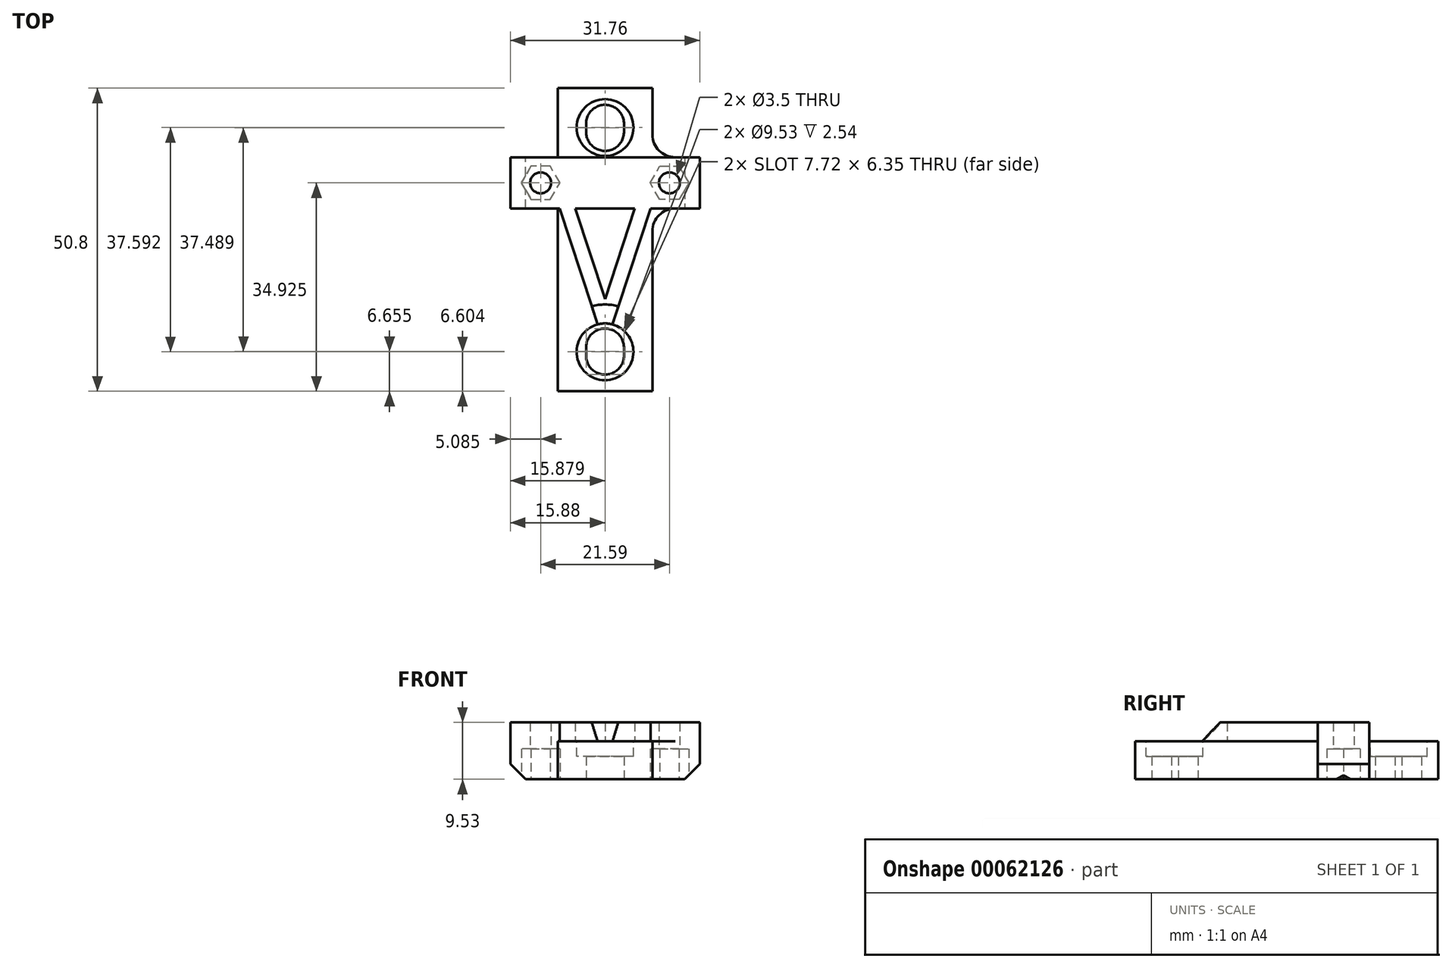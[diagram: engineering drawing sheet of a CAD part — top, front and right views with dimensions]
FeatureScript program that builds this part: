
annotation { "Feature Type Name" : "Feature", "Feature Type Description" : "" }
export const myFeature = defineFeature(function(context is Context, id is Id, definition is map)
    precondition{}
    {
        {
            var Q0;
            Q0=qCreatedBy(makeId("Top.planeOp"),FACE);
            var sketch = newSketch(context, id + "F0", { "sketchPlane" : qUnion([Q0])});
            skLineSegment(sketch, "E0.bottom", {"start": v(-7.94, 25.4) * mm, "end": v(7.94, 25.4) * mm});
            skLineSegment(sketch, "E0.top", {"start": v(-7.94, -25.4) * mm, "end": v(7.94, -25.4) * mm});
            skLineSegment(sketch, "E0.left", {"start": v(-7.94, 25.4) * mm, "end": v(-7.94, -25.4) * mm});
            skLineSegment(sketch, "E0.right", {"start": v(7.94, 25.4) * mm, "end": v(7.94, -25.4) * mm});
            skPoint(sketch, "E1", {"position": v(0, 18.8) * mm});
            skPoint(sketch, "E2", {"position": v(0, -18.8) * mm});
            skLineSegment(sketch, "E3", {"start": v(3.17, -18.16) * mm, "end": v(3.17, -19.43) * mm});
            skArc(sketch, "E4", {"start": v(3.17, -19.43) * mm, "mid": v(-0.05, -22.6) * mm, "end": v(-3.17, -19.33) * mm});
            skLineSegment(sketch, "E5", {"start": v(0, -28.7) * mm, "end": v(0, 36.3) * mm, "construction": true});
            skLineSegment(sketch, "E6", {"start": v(-3.17, -19.33) * mm, "end": v(-3.17, -18.06) * mm});
            skArc(sketch, "E7", {"start": v(-3.17, -18.06) * mm, "mid": v(0.05, -14.88) * mm, "end": v(3.17, -18.16) * mm});
            skLineSegment(sketch, "E8.MirrorCS", {"start": v(-7.94, -25.4) * mm, "end": v(-7.94, 25.4) * mm});
            skArc(sketch, "E9.MirrorCS", {"start": v(-3.17, 18.06) * mm, "mid": v(0.05, 14.88) * mm, "end": v(3.17, 18.16) * mm});
            skLineSegment(sketch, "E10.MirrorCS", {"start": v(-3.17, 19.33) * mm, "end": v(-3.17, 18.06) * mm});
            skArc(sketch, "E11.MirrorCS", {"start": v(3.17, 19.43) * mm, "mid": v(-0.05, 22.6) * mm, "end": v(-3.17, 19.33) * mm});
            skLineSegment(sketch, "E12.MirrorCS", {"start": v(3.17, 18.16) * mm, "end": v(3.17, 19.43) * mm});
            skSolve(sketch);
        }
        {
            var Q0;
            Q0 = qSketchRegion(id + "F0", true);
            extrude(context, id + "F1", {"entities" : qUnion([Q0]), "depth" : 6.35 * mm});
        }
        {
            var Q0;
            Q0=makeQuery(id+"F1.opExtrude","CAP_FACE",FACE,{"disambiguationData":[OSD([sQuery(id+"F0.wireOp",EDGE,"E0.bottom"),sQuery(id+"F0.wireOp",EDGE,"E0.top"),sQuery(id+"F0.wireOp",EDGE,"E0.left"),sQuery(id+"F0.wireOp",EDGE,"E0.right"),sQuery(id+"F0.wireOp",EDGE,"db3065ad-5405-4db5-aa4e-17a35d9fe363"),sQuery(id+"F0.wireOp",EDGE,"fdb6fcd1-f64e-4614-bf4e-cf34bd7a5e28")])],"isStart":false});
            var sketch = newSketch(context, id + "F2", { "sketchPlane" : qUnion([Q0])});
            skLineSegment(sketch, "E13.bottom", {"start": v(-15.88, 13.83) * mm, "end": v(15.88, 13.83) * mm});
            skLineSegment(sketch, "E13.top", {"start": v(-15.87, 5.23) * mm, "end": v(15.87, 5.23) * mm});
            skLineSegment(sketch, "E13.left", {"start": v(-15.88, 13.83) * mm, "end": v(-15.88, 5.22) * mm});
            skLineSegment(sketch, "E13.right", {"start": v(15.88, 13.83) * mm, "end": v(15.88, 5.22) * mm});
            skLineSegment(sketch, "E14", {"start": v(-31.76, 9.52) * mm, "end": v(36.02, 9.53) * mm, "construction": true});
            skCircle(sketch, "E15", {"center": v(-10.8, 9.52) * mm, "radius": 1.75 * mm});
            skCircle(sketch, "E16", {"center": v(10.8, 9.52) * mm, "radius": 1.75 * mm});
            skSolve(sketch);
        }
        {
            var Q0;
            Q0 = qSketchRegion(id + "F2", true);
            var Q1;
            Q1=makeQuery(id+"F1.opExtrude","CAP_FACE",FACE,{"disambiguationData":[OSD([sQuery(id+"F0.wireOp",EDGE,"E0.bottom"),sQuery(id+"F0.wireOp",EDGE,"E0.top"),sQuery(id+"F0.wireOp",EDGE,"E0.left"),sQuery(id+"F0.wireOp",EDGE,"E0.right"),sQuery(id+"F0.wireOp",EDGE,"db3065ad-5405-4db5-aa4e-17a35d9fe363"),sQuery(id+"F0.wireOp",EDGE,"fdb6fcd1-f64e-4614-bf4e-cf34bd7a5e28")])],"isStart":true});
            extrude(context, id + "F3", {"entities" : qUnion([Q0]), "operationType" : NewBodyOperationType.ADD, "depth" : 3.17 * mm, "hasSecondDirection" : true, "secondDirectionBound" : SecondDirectionBoundingType.UP_TO_SURFACE, "secondDirectionOppositeDirection" : true, "secondDirectionBoundEntityFace" : qUnion([Q1]), "secondDirectionDepth" : 25.4 * mm});
        }
        {
            var Q0;
            {var subQ0=sQuery(id+"F0.wireOp",EDGE,"E3");var subQ1=sQuery(id+"F0.wireOp",EDGE,"E0.right");var subQ2=sQuery(id+"F0.wireOp",EDGE,"E4");var subQ3=sQuery(id+"F0.wireOp",EDGE,"E0.top");var subQ4=sQuery(id+"F0.wireOp",EDGE,"E6");var subQ5=sQuery(id+"F0.wireOp",EDGE,"E7");var subQ6=sQuery(id+"F0.wireOp",EDGE,"E8.MirrorCS");Q0=makeQuery(id+"F3.boolean.opBoolean","SPLIT",FACE,{"disambiguationData":[TD([makeQuery(id+"F1.opExtrude","SWEPT_FACE",FACE,{"disambiguationData":[OSD([subQ3])]})])],"derivedFrom":makeQuery(id+"F1.opExtrude","CAP_FACE",FACE,{"disambiguationData":[OSD([subQ3,subQ1,subQ0,subQ2,subQ4,subQ5,subQ6,sQuery(id+"F0.wireOp",EDGE,"E0.bottom"),sQuery(id+"F0.wireOp",EDGE,"E9.MirrorCS"),sQuery(id+"F0.wireOp",EDGE,"E10.MirrorCS"),sQuery(id+"F0.wireOp",EDGE,"E11.MirrorCS"),sQuery(id+"F0.wireOp",EDGE,"E12.MirrorCS")])],"isStart":false})});}
            var sketch = newSketch(context, id + "F4", { "sketchPlane" : qUnion([Q0])});
            skCircle(sketch, "E17", {"center": v(0, -18.8) * mm, "radius": 4.76 * mm});
            skCircle(sketch, "E18", {"center": v(0, 18.8) * mm, "radius": 4.76 * mm});
            skSolve(sketch);
        }
        {
            var Q0;
            Q0 = qSketchRegion(id + "F4", true);
            extrude(context, id + "F5", {"entities" : qUnion([Q0]), "operationType" : NewBodyOperationType.REMOVE, "oppositeDirection" : true, "depth" : 2.54 * mm});
        }
        {
            var Q0;
            Q0=makeQuery(id+"F3.opExtrude","CAP_EDGE",EDGE,{"disambiguationData":[OSD([sQuery(id+"F2.wireOp",EDGE,"E13.left")])],"isStart":true});
            var Q1;
            Q1=makeQuery(id+"F3.opExtrude","CAP_EDGE",EDGE,{"disambiguationData":[OSD([sQuery(id+"F2.wireOp",EDGE,"E13.right")])],"isStart":true});
            chamfer(context, id + "F6", {"entities" : qUnion([Q0, Q1]), "width" : 2.54 * mm, "tangentPropagation" : true});
        }
        {
            var Q0;
            Q0=makeQuery(id+"F3.boolean.opBoolean","MERGE",FACE,{"derivedFrom":[makeQuery(id+"F1.opExtrude","CAP_FACE",FACE,{"disambiguationData":[OSD([sQuery(id+"F0.wireOp",EDGE,"E0.top"),sQuery(id+"F0.wireOp",EDGE,"E0.right"),sQuery(id+"F0.wireOp",EDGE,"E3"),sQuery(id+"F0.wireOp",EDGE,"E4"),sQuery(id+"F0.wireOp",EDGE,"E6"),sQuery(id+"F0.wireOp",EDGE,"E7"),sQuery(id+"F0.wireOp",EDGE,"E8.MirrorCS"),sQuery(id+"F0.wireOp",EDGE,"E0.bottom"),sQuery(id+"F0.wireOp",EDGE,"E9.MirrorCS"),sQuery(id+"F0.wireOp",EDGE,"E10.MirrorCS"),sQuery(id+"F0.wireOp",EDGE,"E11.MirrorCS"),sQuery(id+"F0.wireOp",EDGE,"E12.MirrorCS")])],"isStart":true}),makeQuery(id+"F3.opExtrude","CAP_FACE",FACE,{"disambiguationData":[OSD([sQuery(id+"F2.wireOp",EDGE,"E13.bottom"),sQuery(id+"F2.wireOp",EDGE,"E13.top"),sQuery(id+"F2.wireOp",EDGE,"E13.left"),sQuery(id+"F2.wireOp",EDGE,"E13.right"),sQuery(id+"F2.wireOp",EDGE,"E15"),sQuery(id+"F2.wireOp",EDGE,"E16")])],"isStart":true})]});
            var sketch = newSketch(context, id + "F7", { "sketchPlane" : qUnion([Q0])});
            skCircle(sketch, "E19.cCircle", {"center": v(-10.8, -9.52) * mm, "radius": 2.8 * mm, "construction": true});
            skLineSegment(sketch, "E19.0", {"start": v(-7.57, -9.53) * mm, "end": v(-9.18, -12.32) * mm});
            skLineSegment(sketch, "E19.1", {"start": v(-9.18, -12.32) * mm, "end": v(-12.4, -12.32) * mm});
            skLineSegment(sketch, "E19.2", {"start": v(-12.4, -12.32) * mm, "end": v(-14.02, -9.52) * mm});
            skLineSegment(sketch, "E19.3", {"start": v(-14.02, -9.52) * mm, "end": v(-12.4, -6.73) * mm});
            skLineSegment(sketch, "E19.4", {"start": v(-12.4, -6.73) * mm, "end": v(-9.18, -6.73) * mm});
            skLineSegment(sketch, "E19.5", {"start": v(-9.18, -6.73) * mm, "end": v(-7.57, -9.53) * mm});
            skPoint(sketch, "E19.0.midPoint", {"position": v(-8.38, -10.92) * mm});
            skLineSegment(sketch, "E20.MirrorCS", {"start": v(9.18, -6.73) * mm, "end": v(7.57, -9.53) * mm});
            skLineSegment(sketch, "E21.MirrorCS", {"start": v(12.4, -6.73) * mm, "end": v(9.18, -6.73) * mm});
            skLineSegment(sketch, "E22.MirrorCS", {"start": v(14.02, -9.52) * mm, "end": v(12.4, -6.73) * mm});
            skLineSegment(sketch, "E23.MirrorCS", {"start": v(12.4, -12.32) * mm, "end": v(14.02, -9.52) * mm});
            skLineSegment(sketch, "E24.MirrorCS", {"start": v(9.18, -12.32) * mm, "end": v(12.4, -12.32) * mm});
            skLineSegment(sketch, "E25.MirrorCS", {"start": v(7.57, -9.53) * mm, "end": v(9.18, -12.32) * mm});
            skCircle(sketch, "E26.MirrorC", {"center": v(10.8, -9.52) * mm, "radius": 2.8 * mm, "construction": true});
            skSolve(sketch);
        }
        {
            var Q0;
            Q0 = qSketchRegion(id + "F7", true);
            extrude(context, id + "F8", {"entities" : qUnion([Q0]), "operationType" : NewBodyOperationType.REMOVE, "oppositeDirection" : true, "depth" : 5.08 * mm});
        }
        {
            var Q0;
            Q0=makeQuery(id+"F3.boolean.opBoolean","INTERSECT",EDGE,{"derivedFrom":[makeQuery(id+"F1.opExtrude","SWEPT_FACE",FACE,{"disambiguationData":[OSD([sQuery(id+"F0.wireOp",EDGE,"E8.MirrorCS")])]}),makeQuery(id+"F3.opExtrude","SWEPT_FACE",FACE,{"disambiguationData":[OSD([sQuery(id+"F2.wireOp",EDGE,"E13.top")])]})]});
            var Q1;
            Q1=makeQuery(id+"F3.boolean.opBoolean","INTERSECT",EDGE,{"derivedFrom":[makeQuery(id+"F1.opExtrude","SWEPT_FACE",FACE,{"disambiguationData":[OSD([sQuery(id+"F0.wireOp",EDGE,"E0.right")])]}),makeQuery(id+"F3.opExtrude","SWEPT_FACE",FACE,{"disambiguationData":[OSD([sQuery(id+"F2.wireOp",EDGE,"E13.top")])]})]});
            var Q2;
            Q2=makeQuery(id+"F3.boolean.opBoolean","INTERSECT",EDGE,{"derivedFrom":[makeQuery(id+"F1.opExtrude","SWEPT_FACE",FACE,{"disambiguationData":[OSD([sQuery(id+"F0.wireOp",EDGE,"E0.right")])]}),makeQuery(id+"F3.opExtrude","SWEPT_FACE",FACE,{"disambiguationData":[OSD([sQuery(id+"F2.wireOp",EDGE,"E13.bottom")])]})]});
            var Q3;
            Q3=makeQuery(id+"F3.boolean.opBoolean","INTERSECT",EDGE,{"derivedFrom":[makeQuery(id+"F1.opExtrude","SWEPT_FACE",FACE,{"disambiguationData":[OSD([sQuery(id+"F0.wireOp",EDGE,"E8.MirrorCS")])]}),makeQuery(id+"F3.opExtrude","SWEPT_FACE",FACE,{"disambiguationData":[OSD([sQuery(id+"F2.wireOp",EDGE,"E13.bottom")])]})]});
            fillet(context, id + "F9", {"entities" : qUnion([Q0, Q1, Q2, Q3]), "radius" : 3.8 * mm, "tangentPropagation" : true, "allowEdgeOverflow" : false});
        }
        {
            var Q0;
            {var subQ0=sQuery(id+"F0.wireOp",EDGE,"E3");var subQ1=sQuery(id+"F0.wireOp",EDGE,"E0.right");var subQ2=sQuery(id+"F0.wireOp",EDGE,"E4");var subQ3=sQuery(id+"F0.wireOp",EDGE,"E0.top");var subQ4=sQuery(id+"F0.wireOp",EDGE,"E6");var subQ5=sQuery(id+"F0.wireOp",EDGE,"E7");var subQ6=sQuery(id+"F0.wireOp",EDGE,"E8.MirrorCS");Q0=makeQuery(id+"F3.boolean.opBoolean","SPLIT",FACE,{"disambiguationData":[TD([makeQuery(id+"F1.opExtrude","SWEPT_FACE",FACE,{"disambiguationData":[OSD([subQ3])]})])],"derivedFrom":makeQuery(id+"F1.opExtrude","CAP_FACE",FACE,{"disambiguationData":[OSD([subQ3,subQ1,subQ0,subQ2,subQ4,subQ5,subQ6,sQuery(id+"F0.wireOp",EDGE,"E0.bottom"),sQuery(id+"F0.wireOp",EDGE,"E9.MirrorCS"),sQuery(id+"F0.wireOp",EDGE,"E10.MirrorCS"),sQuery(id+"F0.wireOp",EDGE,"E11.MirrorCS"),sQuery(id+"F0.wireOp",EDGE,"E12.MirrorCS")])],"isStart":false})});}
            var sketch = newSketch(context, id + "F10", { "sketchPlane" : qUnion([Q0])});
            skLineSegment(sketch, "E27", {"start": v(-7.63, 5.23) * mm, "end": v(-1.23, -14.2) * mm});
            skLineSegment(sketch, "E28", {"start": v(-7.63, 5.23) * mm, "end": v(-5, 5.23) * mm});
            skLineSegment(sketch, "E29", {"start": v(-5, 5.23) * mm, "end": v(0, -9.95) * mm});
            skArc(sketch, "E30.0", {"start": v(1.23, -14.2) * mm, "mid": v(0, -14.03) * mm, "end": v(-1.23, -14.2) * mm});
            skLineSegment(sketch, "E31.MirrorCS", {"start": v(5, 5.23) * mm, "end": v(0, -9.95) * mm});
            skLineSegment(sketch, "E32.MirrorCS", {"start": v(7.63, 5.23) * mm, "end": v(5, 5.23) * mm});
            skLineSegment(sketch, "E33.MirrorCS", {"start": v(7.63, 5.23) * mm, "end": v(1.23, -14.2) * mm});
            skSolve(sketch);
        }
        {
            var Q0;
            Q0 = qSketchRegion(id + "F10", true);
            var Q1;
            Q1=makeQuery(id+"F3.opExtrude","CAP_FACE",FACE,{"disambiguationData":[OSD([sQuery(id+"F2.wireOp",EDGE,"E13.bottom"),sQuery(id+"F2.wireOp",EDGE,"E13.top"),sQuery(id+"F2.wireOp",EDGE,"E13.left"),sQuery(id+"F2.wireOp",EDGE,"E13.right"),sQuery(id+"F2.wireOp",EDGE,"E15"),sQuery(id+"F2.wireOp",EDGE,"E16")])],"isStart":false});
            extrude(context, id + "F11", {"entities" : qUnion([Q0]), "operationType" : NewBodyOperationType.ADD, "endBound" : BoundingType.UP_TO_SURFACE, "endBoundEntityFace" : qUnion([Q1]), "depth" : 25 * mm});
        }
        {
            var Q0;
            Q0=makeQuery(id+"F11.opExtrude","CAP_EDGE",EDGE,{"disambiguationData":[OSD([sQuery(id+"F10.wireOp",EDGE,"E30.0")])],"isStart":false});
            chamfer(context, id + "F12", {"entities" : qUnion([Q0]), "width" : 3.17 * mm, "tangentPropagation" : true});
        }
    });
